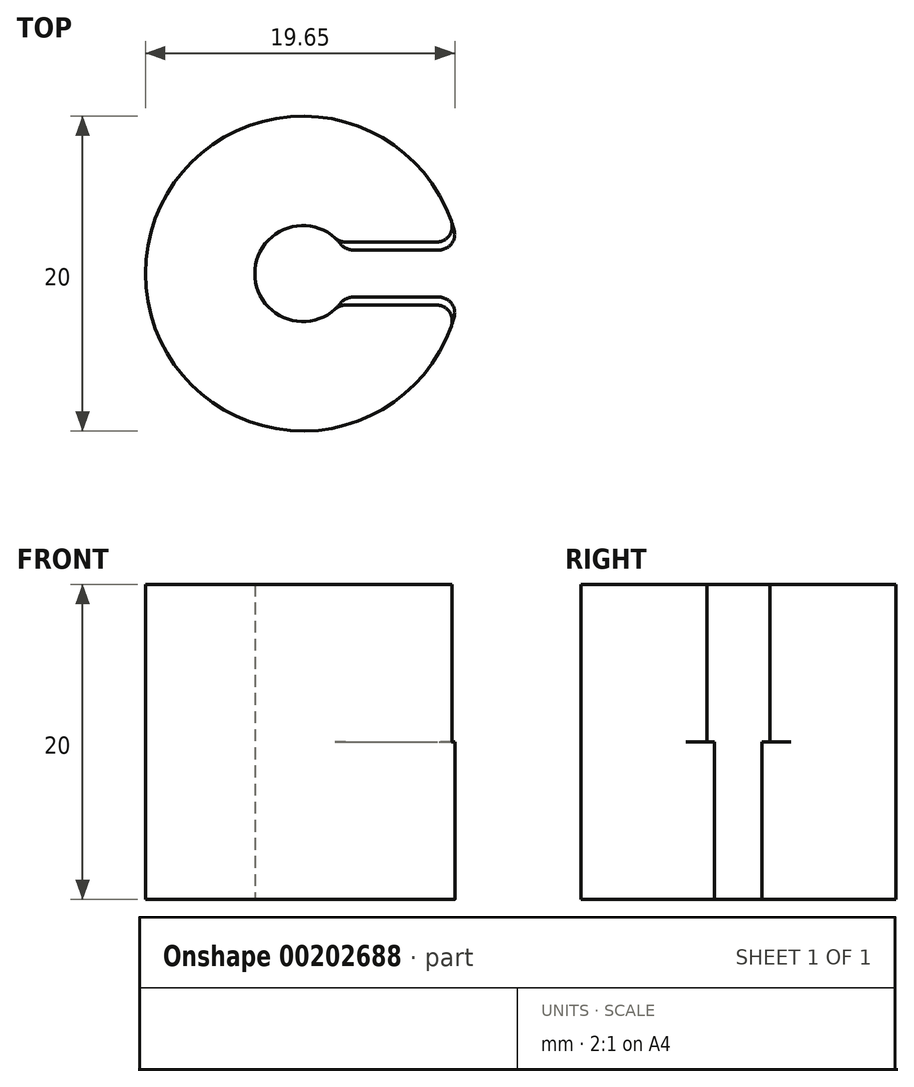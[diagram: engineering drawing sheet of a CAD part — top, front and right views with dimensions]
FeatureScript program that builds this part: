
annotation { "Feature Type Name" : "Feature", "Feature Type Description" : "" }
export const myFeature = defineFeature(function(context is Context, id is Id, definition is map)
    precondition{}
    {
        {
            var Q0;
            Q0=qCreatedBy(makeId("Top.planeOp"),FACE);
            var sketch = newSketch(context, id + "F0", { "sketchPlane" : qUnion([Q0])});
            skArc(sketch, "E0", {"start": v(9.8, 2) * mm, "mid": v(-10, 0) * mm, "end": v(9.8, -2) * mm});
            skArc(sketch, "E1", {"start": v(2.3, 2) * mm, "mid": v(-3.05, 0) * mm, "end": v(2.3, -2) * mm});
            skLineSegment(sketch, "E2.trimOffspring", {"start": v(2.3, -2) * mm, "end": v(9.8, -2) * mm});
            skLineSegment(sketch, "E3.trimOffspring", {"start": v(2.3, 2) * mm, "end": v(9.8, 2) * mm});
            skSolve(sketch);
        }
        {
            var Q0;
            Q0=makeQuery(id+"F0.imprint","IMPRINT",FACE,{"disambiguationData":[TD([[makeQuery(id+"F0.imprint","IMPRINT",EDGE,{"derivedFrom":sQuery(id+"F0.wireOp",EDGE,"E0")}),1.0]])]});
            extrude(context, id + "F1", {"entities" : qUnion([Q0]), "depth" : 20 * mm});
        }
        {
            var Q0;
            Q0=makeQuery(id+"F1.opExtrude","SWEPT_EDGE",EDGE,{"disambiguationData":[OSD([sQuery(id+"F0.wireOp",EDGE,"E0"),sQuery(id+"F0.wireOp",EDGE,"E3.trimOffspring")])]});
            var Q1;
            Q1=makeQuery(id+"F1.opExtrude","SWEPT_EDGE",EDGE,{"disambiguationData":[OSD([sQuery(id+"F0.wireOp",EDGE,"E1"),sQuery(id+"F0.wireOp",EDGE,"E3.trimOffspring")])]});
            var Q2;
            Q2=makeQuery(id+"F1.opExtrude","SWEPT_EDGE",EDGE,{"disambiguationData":[OSD([sQuery(id+"F0.wireOp",EDGE,"E1"),sQuery(id+"F0.wireOp",EDGE,"E2.trimOffspring")])]});
            var Q3;
            Q3=makeQuery(id+"F1.opExtrude","SWEPT_EDGE",EDGE,{"disambiguationData":[OSD([sQuery(id+"F0.wireOp",EDGE,"E0"),sQuery(id+"F0.wireOp",EDGE,"E2.trimOffspring")])]});
            fillet(context, id + "F2", {"entities" : qUnion([Q0, Q1, Q2, Q3]), "radius" : 1 * mm, "allowEdgeOverflow" : false});
        }
        {
            var Q0;
            Q0=qCreatedBy(makeId("Top.planeOp"),FACE);
            var sketch = newSketch(context, id + "F3", { "sketchPlane" : qUnion([Q0])});
            skArc(sketch, "E4", {"start": v(9.89, 1.5) * mm, "mid": v(-10, 0) * mm, "end": v(9.89, -1.5) * mm});
            skArc(sketch, "E5", {"start": v(2.66, 1.5) * mm, "mid": v(-3.05, 0) * mm, "end": v(2.66, -1.5) * mm});
            skLineSegment(sketch, "E6.trimOffspring", {"start": v(2.66, -1.5) * mm, "end": v(9.89, -1.5) * mm});
            skLineSegment(sketch, "E7.trimOffspring", {"start": v(2.66, 1.5) * mm, "end": v(9.89, 1.5) * mm});
            skSolve(sketch);
        }
        {
            var Q0;
            Q0=qSketchRegion(id+"F3",true);
            var Q1;
            Q1=makeQuery(id+"F1.opExtrude","CAP_FACE",FACE,{"disambiguationData":[OSD([sQuery(id+"F0.wireOp",EDGE,"E0"),sQuery(id+"F0.wireOp",EDGE,"E1"),sQuery(id+"F0.wireOp",EDGE,"E2.trimOffspring"),sQuery(id+"F0.wireOp",EDGE,"E3.trimOffspring")])],"isStart":false});
            extrude(context, id + "F4", {"entities" : qUnion([Q0]), "operationType" : NewBodyOperationType.ADD, "depth" : 10 * mm});
        }
        {
            var Q0;
            Q0=makeQuery(id+"F4.opExtrude","SWEPT_EDGE",EDGE,{"disambiguationData":[OSD([sQuery(id+"F3.wireOp",EDGE,"E4"),sQuery(id+"F3.wireOp",EDGE,"E6.trimOffspring")])]});
            var Q1;
            Q1=makeQuery(id+"F4.opExtrude","SWEPT_EDGE",EDGE,{"disambiguationData":[OSD([sQuery(id+"F3.wireOp",EDGE,"E4"),sQuery(id+"F3.wireOp",EDGE,"E7.trimOffspring")])]});
            var Q2;
            Q2=makeQuery(id+"F4.opExtrude","SWEPT_EDGE",EDGE,{"disambiguationData":[OSD([sQuery(id+"F3.wireOp",EDGE,"E5"),sQuery(id+"F3.wireOp",EDGE,"E6.trimOffspring")])]});
            var Q3;
            Q3=makeQuery(id+"F4.opExtrude","SWEPT_EDGE",EDGE,{"disambiguationData":[OSD([sQuery(id+"F3.wireOp",EDGE,"E5"),sQuery(id+"F3.wireOp",EDGE,"E7.trimOffspring")])]});
            fillet(context, id + "F5", {"entities" : qUnion([Q0, Q1, Q2, Q3]), "radius" : 1 * mm, "tangentPropagation" : true, "allowEdgeOverflow" : false});
        }
    });
